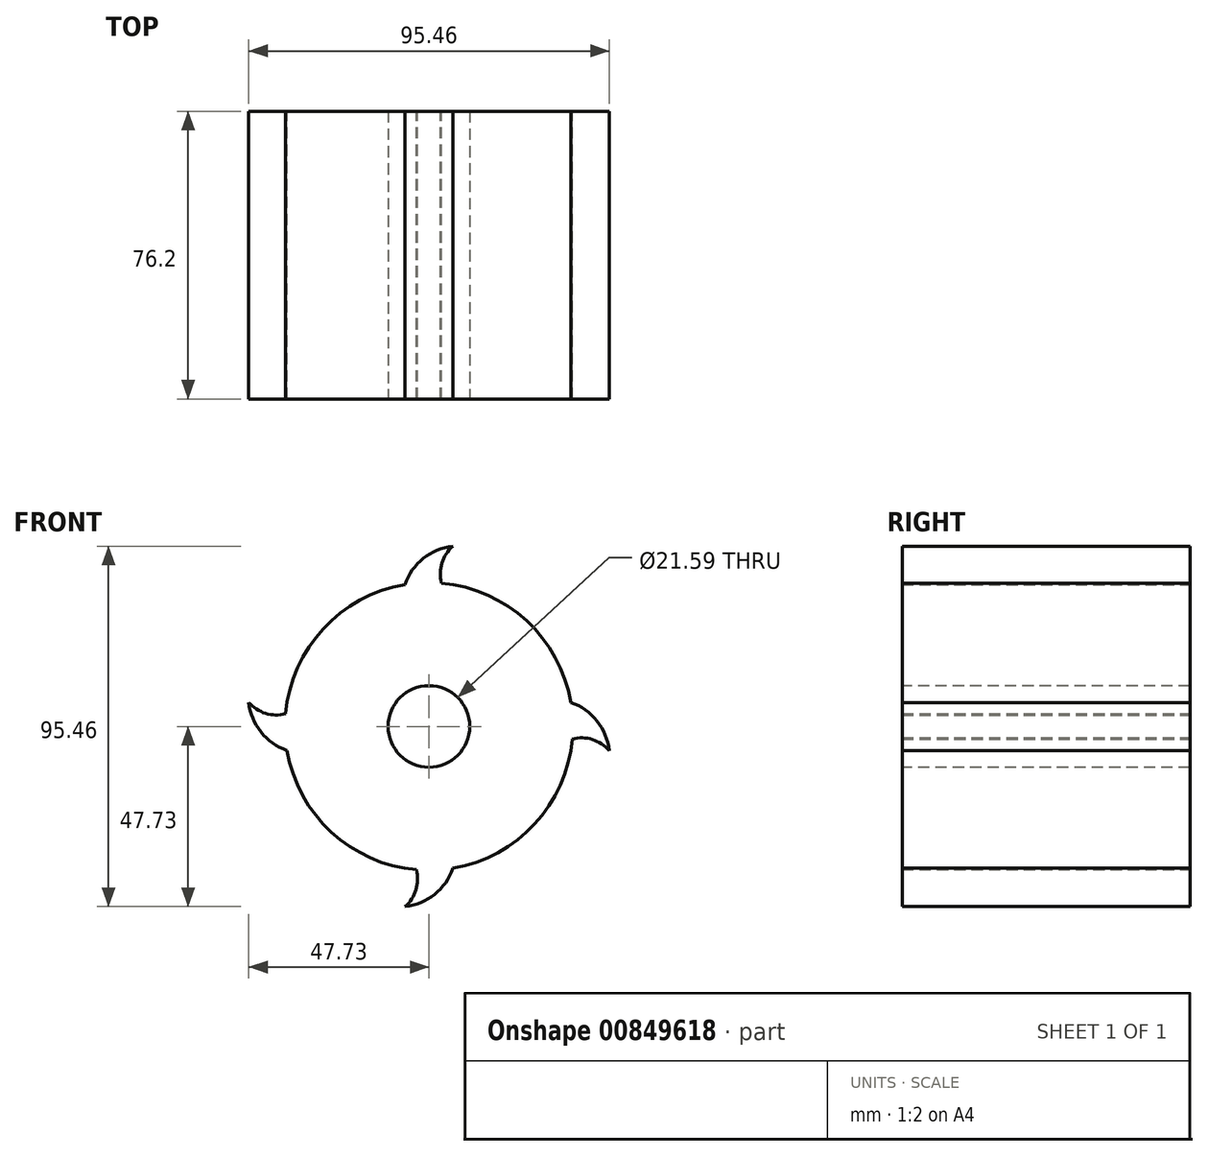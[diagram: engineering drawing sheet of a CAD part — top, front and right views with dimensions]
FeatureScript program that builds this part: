
annotation { "Feature Type Name" : "Feature", "Feature Type Description" : "" }
export const myFeature = defineFeature(function(context is Context, id is Id, definition is map)
    precondition{}
    {
        {
            var Q0;
            Q0=qCreatedBy(makeId("Front.planeOp"),FACE);
            var sketch = newSketch(context, id + "F0", { "sketchPlane" : qUnion([Q0])});
            skCircle(sketch, "E0", {"center": v(0, 0) * mm, "radius": 38.1 * mm});
            skLineSegment(sketch, "E1", {"start": v(-37.57, -6.35) * mm, "end": v(-47.73, -6.35) * mm});
            skLineSegment(sketch, "E2", {"start": v(-37.57, 6.35) * mm, "end": v(-47.73, 6.35) * mm});
            skArc(sketch, "E3", {"start": v(-47.73, 6.35) * mm, "mid": v(-44.5, -1.48) * mm, "end": v(-37.57, -6.35) * mm});
            skArc(sketch, "E4", {"start": v(-47.73, 6.35) * mm, "mid": v(-43.27, 3.46) * mm, "end": v(-37.95, 3.34) * mm});
            skArc(sketch, "E5.1.0", {"start": v(-6.35, -47.73) * mm, "mid": v(-3.46, -43.27) * mm, "end": v(-3.34, -37.95) * mm});
            skArc(sketch, "E5.1.1", {"start": v(-6.35, -47.73) * mm, "mid": v(1.48, -44.5) * mm, "end": v(6.35, -37.57) * mm});
            skArc(sketch, "E5.2.0", {"start": v(47.73, -6.35) * mm, "mid": v(43.27, -3.46) * mm, "end": v(37.95, -3.34) * mm});
            skArc(sketch, "E5.2.1", {"start": v(47.73, -6.35) * mm, "mid": v(44.5, 1.48) * mm, "end": v(37.57, 6.35) * mm});
            skArc(sketch, "E5.3.0", {"start": v(6.35, 47.73) * mm, "mid": v(3.46, 43.27) * mm, "end": v(3.34, 37.95) * mm});
            skArc(sketch, "E5.3.1", {"start": v(6.35, 47.73) * mm, "mid": v(-1.48, 44.5) * mm, "end": v(-6.35, 37.57) * mm});
            skSolve(sketch);
        }
        {
            var Q0;
            {var subQ0=sQuery(id+"F0.wireOp",EDGE,"E5.3.0");Q0=makeQuery(id+"F0.imprint","IMPRINT",FACE,{"disambiguationData":[TD([[makeQuery(id+"F0.imprint","IMPRINT",EDGE,{"derivedFrom":subQ0}),-1.0]])]});}
            var Q1;
            {var subQ0=sQuery(id+"F0.wireOp",EDGE,"E0");var subQ5=makeQuery(id+"F0.imprint","INTERSECT",VERTEX,{"derivedFrom":[subQ0,sQuery(id+"F0.wireOp",EDGE,"E5.2.1")]});Q1=makeQuery(id+"F0.imprint","IMPRINT",FACE,{"disambiguationData":[TD([[makeQuery(id+"F0.imprint","IMPRINT",EDGE,{"disambiguationData":[TD([[subQ5,-1.0]])],"derivedFrom":subQ0}),1.0]])]});}
            var Q2;
            {var subQ0=sQuery(id+"F0.wireOp",EDGE,"E3");Q2=makeQuery(id+"F0.imprint","IMPRINT",FACE,{"disambiguationData":[TD([[makeQuery(id+"F0.imprint","IMPRINT",EDGE,{"derivedFrom":subQ0}),1.0]])]});}
            var Q3;
            {var subQ0=sQuery(id+"F0.wireOp",EDGE,"E5.2.0");Q3=makeQuery(id+"F0.imprint","IMPRINT",FACE,{"disambiguationData":[TD([[makeQuery(id+"F0.imprint","IMPRINT",EDGE,{"derivedFrom":subQ0}),-1.0]])]});}
            var Q4;
            {var subQ0=sQuery(id+"F0.wireOp",EDGE,"E5.1.0");Q4=makeQuery(id+"F0.imprint","IMPRINT",FACE,{"disambiguationData":[TD([[makeQuery(id+"F0.imprint","IMPRINT",EDGE,{"derivedFrom":subQ0}),-1.0]])]});}
            extrude(context, id + "F1", {"entities" : qUnion([Q0, Q1, Q2, Q3, Q4]), "depth" : 76.2 * mm, "offsetDistance" : 25.4 * mm});
        }
        {
            var Q0;
            Q0=makeQuery(id+"F1.opExtrude","CAP_FACE",FACE,{"disambiguationData":[OSD([sQuery(id+"F0.wireOp",EDGE,"E0"),sQuery(id+"F0.wireOp",EDGE,"E3"),sQuery(id+"F0.wireOp",EDGE,"E4"),sQuery(id+"F0.wireOp",EDGE,"E5.1.0"),sQuery(id+"F0.wireOp",EDGE,"E5.1.1"),sQuery(id+"F0.wireOp",EDGE,"E5.2.0"),sQuery(id+"F0.wireOp",EDGE,"E5.2.1"),sQuery(id+"F0.wireOp",EDGE,"E5.3.0"),sQuery(id+"F0.wireOp",EDGE,"E5.3.1")])],"isStart":false});
            var sketch = newSketch(context, id + "F2", { "sketchPlane" : qUnion([Q0])});
            skCircle(sketch, "E6", {"center": v(0, 0) * mm, "radius": 10.8 * mm});
            skSolve(sketch);
        }
        {
            var Q0;
            Q0=makeQuery(id+"F2.imprint","IMPRINT",FACE,{"disambiguationData":[TD([[makeQuery(id+"F2.imprint","IMPRINT",EDGE,{"derivedFrom":sQuery(id+"F2.wireOp",EDGE,"E6")}),1.0]])]});
            extrude(context, id + "F3", {"entities" : qUnion([Q0]), "operationType" : NewBodyOperationType.REMOVE, "endBound" : BoundingType.THROUGH_ALL, "oppositeDirection" : true, "depth" : 25.4 * mm, "offsetDistance" : 25.4 * mm});
        }
    });
